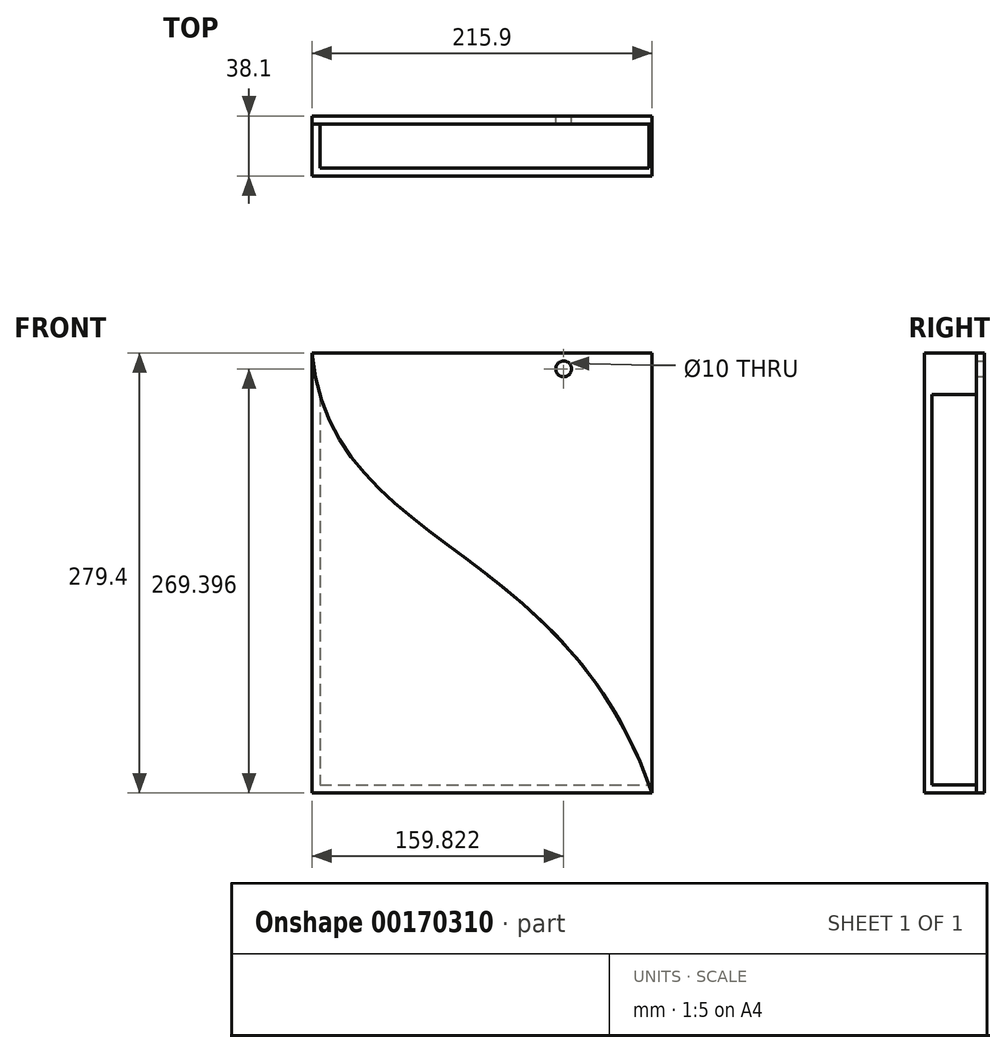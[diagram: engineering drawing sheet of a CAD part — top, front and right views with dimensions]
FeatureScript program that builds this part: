
annotation { "Feature Type Name" : "Feature", "Feature Type Description" : "" }
export const myFeature = defineFeature(function(context is Context, id is Id, definition is map)
    precondition{}
    {
        {
            var Q0;
            Q0=qCreatedBy(makeId("Front.planeOp"),FACE);
            var sketch = newSketch(context, id + "F0", { "sketchPlane" : qUnion([Q0])});
            skLineSegment(sketch, "E0.bottom", {"start": v(-84.91, 181.9) * mm, "end": v(130.99, 181.9) * mm});
            skLineSegment(sketch, "E0.top", {"start": v(-84.91, -97.5) * mm, "end": v(130.99, -97.5) * mm});
            skLineSegment(sketch, "E0.left", {"start": v(-84.91, 181.9) * mm, "end": v(-84.91, -97.5) * mm});
            skLineSegment(sketch, "E0.right", {"start": v(130.99, 181.9) * mm, "end": v(130.99, -97.5) * mm});
            skPoint(sketch, "E0.middle", {"position": v(23.04, 42.2) * mm});
            skFitSpline(sketch, "E1", {"points": [v(-84.91, 181.9) * mm, v(130.99, -97.5) * mm], "startDerivative": vector(36.37, -375.41) * mm, "endDerivative": vector(166.43, -484.3) * mm});
            skSolve(sketch);
        }
        {
            var Q0;
            Q0=makeQuery(id+"F0.imprint","IMPRINT",FACE,{"disambiguationData":[TD([[makeQuery(id+"F0.imprint","IMPRINT",EDGE,{"derivedFrom":sQuery(id+"F0.wireOp",EDGE,"E0.top")}),1.0]])]});
            extrude(context, id + "F1", {"entities" : qUnion([Q0]), "depth" : 38.1 * mm});
        }
        {
            var Q0;
            Q0=makeQuery(id+"F0.imprint","IMPRINT",FACE,{"disambiguationData":[TD([[makeQuery(id+"F0.imprint","IMPRINT",EDGE,{"derivedFrom":sQuery(id+"F0.wireOp",EDGE,"E0.bottom")}),-1.0]])]});
            extrude(context, id + "F2", {"entities" : qUnion([Q0]), "operationType" : NewBodyOperationType.ADD, "depth" : 5 * mm});
        }
        {
            var Q0;
            Q0=makeQuery(id+"F1.opExtrude","SWEPT_FACE",FACE,{"disambiguationData":[OSD([sQuery(id+"F0.wireOp",EDGE,"E1")])]});
            shell(context, id + "F3", {"entities" : qUnion([Q0]), "thickness" : 5 * mm});
        }
        {
            var Q0;
            {var subQ0=sQuery(id+"F0.wireOp",EDGE,"E1");var subQ1=sQuery(id+"F0.wireOp",EDGE,"E0.right");var subQ2=sQuery(id+"F0.wireOp",EDGE,"E0.bottom");Q0=makeQuery(id+"F3.opShell","MERGE",FACE,{"derivedFrom":[makeQuery(id+"F2.opExtrude","CAP_FACE",FACE,{"disambiguationData":[OSD([subQ2,subQ1,subQ0])],"isStart":false}),makeQuery(id+"F2.boolean.opBoolean","MERGE",FACE,{"derivedFrom":[makeQuery(id+"F1.opExtrude","CAP_FACE",FACE,{"disambiguationData":[OSD([sQuery(id+"F0.wireOp",EDGE,"E0.top"),sQuery(id+"F0.wireOp",EDGE,"E0.left"),subQ0])],"isStart":true}),makeQuery(id+"F2.opExtrude","CAP_FACE",FACE,{"disambiguationData":[OSD([subQ2,subQ1,subQ0])],"isStart":true})]})]});}
            var sketch = newSketch(context, id + "F4", { "sketchPlane" : qUnion([Q0])});
            skCircle(sketch, "E2", {"center": v(120.99, 171.9) * mm, "radius": 5 * mm});
            skCircle(sketch, "E3", {"center": v(-74.91, 171.9) * mm, "radius": 5 * mm});
            skSolve(sketch);
        }
        {
            var Q0;
            Q0=makeQuery(id+"F4.imprint","IMPRINT",FACE,{"disambiguationData":[TD([[makeQuery(id+"F4.imprint","IMPRINT",EDGE,{"derivedFrom":sQuery(id+"F4.wireOp",EDGE,"E3")}),1.0]])]});
            var Q1;
            Q1=makeQuery(id+"F4.imprint","IMPRINT",FACE,{"disambiguationData":[TD([[makeQuery(id+"F4.imprint","IMPRINT",EDGE,{"derivedFrom":sQuery(id+"F4.wireOp",EDGE,"E2")}),1.0]])]});
            extrude(context, id + "F5", {"entities" : qUnion([Q0, Q1]), "operationType" : NewBodyOperationType.REMOVE, "oppositeDirection" : true, "depth" : 5 * mm});
        }
        {
            var Q0;
            Q0=qCreatedBy(makeId("Right.planeOp"),FACE);
            var sketch = newSketch(context, id + "F6", { "sketchPlane" : qUnion([Q0])});
            skLineSegment(sketch, "E4.bottom", {"start": v(-33.1, 42.2) * mm, "end": v(-5, 42.2) * mm});
            skLineSegment(sketch, "E4.top", {"start": v(-33.1, -92.5) * mm, "end": v(-5, -92.5) * mm});
            skLineSegment(sketch, "E4.left", {"start": v(-33.1, 42.2) * mm, "end": v(-33.1, -92.5) * mm});
            skLineSegment(sketch, "E4.right", {"start": v(-5, 42.2) * mm, "end": v(-5, -92.5) * mm});
            skSolve(sketch);
        }
        {
            var Q0;
            Q0 = qSketchRegion(id + "F6", true);
            extrude(context, id + "F7", {"entities" : qUnion([Q0]), "operationType" : NewBodyOperationType.REMOVE, "depth" : 152.4 * mm});
        }
    });
